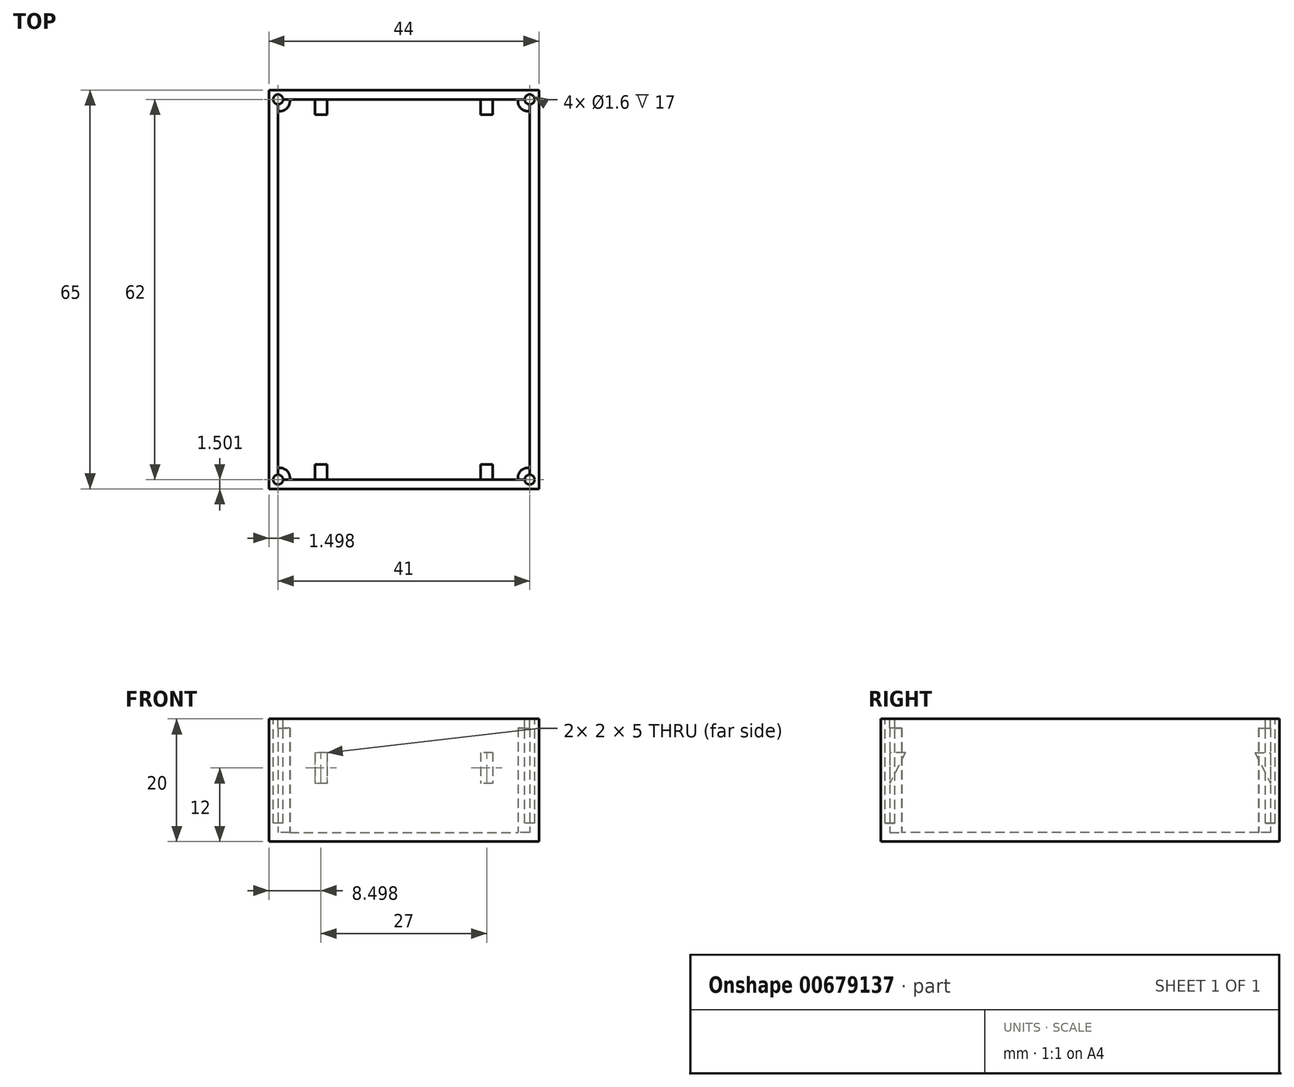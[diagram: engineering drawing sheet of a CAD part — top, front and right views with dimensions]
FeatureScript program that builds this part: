
annotation { "Feature Type Name" : "Feature", "Feature Type Description" : "" }
export const myFeature = defineFeature(function(context is Context, id is Id, definition is map)
    precondition{}
    {
        {
            var Q0;
            Q0=qCreatedBy(makeId("Top.planeOp"),FACE);
            var sketch = newSketch(context, id + "F0", { "sketchPlane" : qUnion([Q0])});
            skLineSegment(sketch, "E0.bottom", {"start": v(-45.45, -34.22) * mm, "end": v(-1.45, -34.22) * mm});
            skLineSegment(sketch, "E0.top", {"start": v(-45.45, -99.22) * mm, "end": v(-1.45, -99.22) * mm});
            skLineSegment(sketch, "E0.left", {"start": v(-45.45, -34.22) * mm, "end": v(-45.45, -99.22) * mm});
            skLineSegment(sketch, "E0.right", {"start": v(-1.45, -34.22) * mm, "end": v(-1.45, -99.22) * mm});
            skSolve(sketch);
        }
        {
            var Q0;
            Q0=makeQuery(id+"F0.imprint","IMPRINT",FACE,{"disambiguationData":[TD([[makeQuery(id+"F0.imprint","IMPRINT",EDGE,{"derivedFrom":sQuery(id+"F0.wireOp",EDGE,"E0.bottom")}),-1.0]])]});
            extrude(context, id + "F1", {"entities" : qUnion([Q0]), "depth" : 20 * mm, "offsetDistance" : 25 * mm});
        }
        {
            var Q0;
            Q0=makeQuery(id+"F1.opExtrude","CAP_FACE",FACE,{"disambiguationData":[OSD([sQuery(id+"F0.wireOp",EDGE,"E0.bottom"),sQuery(id+"F0.wireOp",EDGE,"E0.top"),sQuery(id+"F0.wireOp",EDGE,"E0.left"),sQuery(id+"F0.wireOp",EDGE,"E0.right")])],"isStart":false});
            var sketch = newSketch(context, id + "F2", { "sketchPlane" : qUnion([Q0])});
            skLineSegment(sketch, "E1.bottom", {"start": v(-43.95, -35.72) * mm, "end": v(-2.95, -35.72) * mm});
            skLineSegment(sketch, "E1.top", {"start": v(-43.95, -97.72) * mm, "end": v(-2.95, -97.72) * mm});
            skLineSegment(sketch, "E1.left", {"start": v(-43.95, -35.72) * mm, "end": v(-43.95, -97.72) * mm});
            skLineSegment(sketch, "E1.right", {"start": v(-2.95, -35.72) * mm, "end": v(-2.95, -97.72) * mm});
            skSolve(sketch);
        }
        {
            var Q0;
            Q0 = qSketchRegion(id + "F2", true);
            extrude(context, id + "F3", {"entities" : qUnion([Q0]), "operationType" : NewBodyOperationType.REMOVE, "oppositeDirection" : true, "depth" : 18.5 * mm, "offsetDistance" : 25 * mm});
        }
        {
            var Q0;
            Q0=makeQuery(id+"F3.boolean.opBoolean","COPY",FACE,{"derivedFrom":makeQuery(id+"F3.opExtrude","SWEPT_FACE",FACE,{"disambiguationData":[OSD([sQuery(id+"F2.wireOp",EDGE,"E1.bottom")])]})});
            var sketch = newSketch(context, id + "F4", { "sketchPlane" : qUnion([Q0])});
            skLineSegment(sketch, "E2.bottom", {"start": v(-37.95, 14.5) * mm, "end": v(-35.95, 14.5) * mm});
            skLineSegment(sketch, "E2.top", {"start": v(-37.95, 9.5) * mm, "end": v(-35.95, 9.5) * mm});
            skLineSegment(sketch, "E2.left", {"start": v(-37.95, 14.5) * mm, "end": v(-37.95, 9.5) * mm});
            skLineSegment(sketch, "E2.right", {"start": v(-35.95, 14.5) * mm, "end": v(-35.95, 9.5) * mm});
            skLineSegment(sketch, "E3.bottom", {"start": v(-10.95, 14.5) * mm, "end": v(-8.95, 14.5) * mm});
            skLineSegment(sketch, "E3.top", {"start": v(-10.95, 9.5) * mm, "end": v(-8.95, 9.5) * mm});
            skLineSegment(sketch, "E3.left", {"start": v(-10.95, 14.5) * mm, "end": v(-10.95, 9.5) * mm});
            skLineSegment(sketch, "E3.right", {"start": v(-8.95, 14.5) * mm, "end": v(-8.95, 9.5) * mm});
            skSolve(sketch);
        }
        {
            var Q0;
            Q0 = qSketchRegion(id + "F4", true);
            extrude(context, id + "F5", {"entities" : qUnion([Q0]), "operationType" : NewBodyOperationType.ADD, "depth" : 5 * mm, "offsetDistance" : 25 * mm});
        }
        {
            var Q0;
            Q0=makeQuery(id+"F5.opExtrude","SWEPT_FACE",FACE,{"disambiguationData":[OSD([sQuery(id+"F4.wireOp",EDGE,"E2.left")])]});
            var sketch = newSketch(context, id + "F6", { "sketchPlane" : qUnion([Q0])});
            skLineSegment(sketch, "E4", {"start": v(35.72, 9.5) * mm, "end": v(38.22, 14.5) * mm});
            skLineSegment(sketch, "E5", {"start": v(38.22, 14.5) * mm, "end": v(40.72, 14.5) * mm});
            skLineSegment(sketch, "E6", {"start": v(40.72, 14.5) * mm, "end": v(40.72, 9.5) * mm});
            skLineSegment(sketch, "E7", {"start": v(40.72, 9.5) * mm, "end": v(35.72, 9.5) * mm});
            skSolve(sketch);
        }
        {
            var Q0;
            Q0 = qSketchRegion(id + "F6", true);
            extrude(context, id + "F7", {"entities" : qUnion([Q0]), "operationType" : NewBodyOperationType.REMOVE, "oppositeDirection" : true, "depth" : 30 * mm, "offsetDistance" : 25 * mm});
        }
        {
            var Q0;
            Q0=makeQuery(id+"F3.boolean.opBoolean","COPY",FACE,{"derivedFrom":makeQuery(id+"F3.opExtrude","SWEPT_FACE",FACE,{"disambiguationData":[OSD([sQuery(id+"F2.wireOp",EDGE,"E1.top")])]})});
            var sketch = newSketch(context, id + "F8", { "sketchPlane" : qUnion([Q0])});
            skLineSegment(sketch, "E8.bottom", {"start": v(35.95, 14.5) * mm, "end": v(37.95, 14.5) * mm});
            skLineSegment(sketch, "E8.top", {"start": v(35.95, 9.5) * mm, "end": v(37.95, 9.5) * mm});
            skLineSegment(sketch, "E8.left", {"start": v(35.95, 14.5) * mm, "end": v(35.95, 9.5) * mm});
            skLineSegment(sketch, "E8.right", {"start": v(37.95, 14.5) * mm, "end": v(37.95, 9.5) * mm});
            skLineSegment(sketch, "E9.bottom", {"start": v(8.95, 14.5) * mm, "end": v(10.95, 14.5) * mm});
            skLineSegment(sketch, "E9.top", {"start": v(8.95, 9.5) * mm, "end": v(10.95, 9.5) * mm});
            skLineSegment(sketch, "E9.left", {"start": v(8.95, 14.5) * mm, "end": v(8.95, 9.5) * mm});
            skLineSegment(sketch, "E9.right", {"start": v(10.95, 14.5) * mm, "end": v(10.95, 9.5) * mm});
            skSolve(sketch);
        }
        {
            var Q0;
            Q0 = qSketchRegion(id + "F8", true);
            extrude(context, id + "F9", {"entities" : qUnion([Q0]), "operationType" : NewBodyOperationType.ADD, "depth" : 5 * mm, "offsetDistance" : 25 * mm});
        }
        {
            var Q0;
            Q0=makeQuery(id+"F9.opExtrude","SWEPT_FACE",FACE,{"disambiguationData":[OSD([sQuery(id+"F8.wireOp",EDGE,"E9.left")])]});
            var sketch = newSketch(context, id + "F10", { "sketchPlane" : qUnion([Q0])});
            skLineSegment(sketch, "E10", {"start": v(-97.72, 9.5) * mm, "end": v(-95.22, 14.5) * mm});
            skLineSegment(sketch, "E11", {"start": v(-95.22, 14.5) * mm, "end": v(-92.72, 14.5) * mm});
            skLineSegment(sketch, "E12", {"start": v(-92.72, 14.5) * mm, "end": v(-92.72, 9.5) * mm});
            skLineSegment(sketch, "E13", {"start": v(-92.72, 9.5) * mm, "end": v(-97.72, 9.5) * mm});
            skSolve(sketch);
        }
        {
            var Q0;
            Q0 = qSketchRegion(id + "F10", true);
            extrude(context, id + "F11", {"entities" : qUnion([Q0]), "operationType" : NewBodyOperationType.REMOVE, "oppositeDirection" : true, "depth" : 30 * mm, "offsetDistance" : 25 * mm});
        }
        {
            var Q0;
            Q0=makeQuery(id+"F3.boolean.opBoolean","COPY",FACE,{"derivedFrom":makeQuery(id+"F3.opExtrude","CAP_FACE",FACE,{"disambiguationData":[OSD([sQuery(id+"F2.wireOp",EDGE,"E1.bottom"),sQuery(id+"F2.wireOp",EDGE,"E1.top"),sQuery(id+"F2.wireOp",EDGE,"E1.left"),sQuery(id+"F2.wireOp",EDGE,"E1.right")])],"isStart":false})});
            var sketch = newSketch(context, id + "F13", { "sketchPlane" : qUnion([Q0])});
            skCircle(sketch, "E14", {"center": v(-43.65, -36.02) * mm, "radius": 1.63 * mm});
            skCircle(sketch, "E15", {"center": v(-3.25, -36.02) * mm, "radius": 1.63 * mm});
            skCircle(sketch, "E16", {"center": v(-3.25, -97.42) * mm, "radius": 1.63 * mm});
            skCircle(sketch, "E17", {"center": v(-43.65, -97.42) * mm, "radius": 1.63 * mm});
            skSolve(sketch);
        }
        {
            var Q0;
            Q0 = qSketchRegion(id + "F13", true);
            extrude(context, id + "F14", {"entities" : qUnion([Q0]), "operationType" : NewBodyOperationType.ADD, "depth" : 17 * mm, "offsetDistance" : 25 * mm});
        }
        {
            var Q0;
            Q0=makeQuery(id+"F1.opExtrude","CAP_FACE",FACE,{"disambiguationData":[OSD([sQuery(id+"F0.wireOp",EDGE,"E0.bottom"),sQuery(id+"F0.wireOp",EDGE,"E0.top"),sQuery(id+"F0.wireOp",EDGE,"E0.left"),sQuery(id+"F0.wireOp",EDGE,"E0.right")])],"isStart":false});
            var sketch = newSketch(context, id + "F15", { "sketchPlane" : qUnion([Q0])});
            skCircle(sketch, "E18", {"center": v(-43.95, -97.72) * mm, "radius": 0.8 * mm});
            skCircle(sketch, "E19", {"center": v(-2.95, -97.72) * mm, "radius": 0.8 * mm});
            skCircle(sketch, "E20", {"center": v(-43.95, -35.72) * mm, "radius": 0.8 * mm});
            skCircle(sketch, "E21", {"center": v(-2.95, -35.72) * mm, "radius": 0.8 * mm});
            skSolve(sketch);
        }
        {
            var Q0;
            Q0 = qSketchRegion(id + "F15", true);
            extrude(context, id + "F16", {"entities" : qUnion([Q0]), "operationType" : NewBodyOperationType.REMOVE, "oppositeDirection" : true, "depth" : 17 * mm, "offsetDistance" : 25 * mm});
        }
    });
